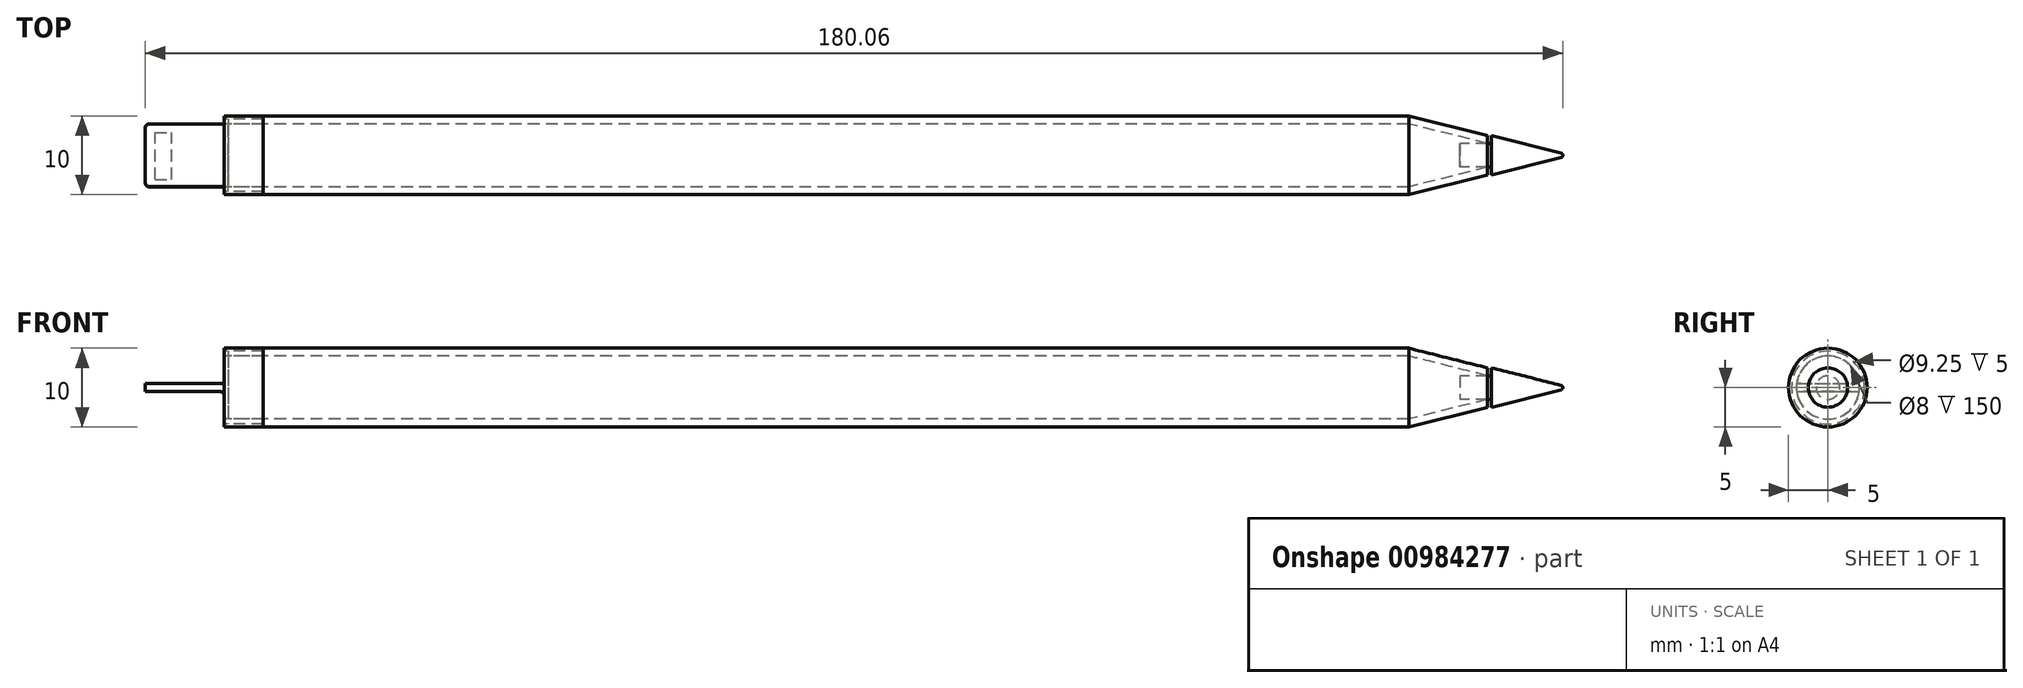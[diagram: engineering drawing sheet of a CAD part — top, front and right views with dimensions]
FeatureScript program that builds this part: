
annotation { "Feature Type Name" : "Feature", "Feature Type Description" : "" }
export const myFeature = defineFeature(function(context is Context, id is Id, definition is map)
    precondition{}
    {
        {
            var Q0;
            Q0=qCreatedBy(makeId("Front.planeOp"),FACE);
            var sketch = newSketch(context, id + "F0", { "sketchPlane" : qUnion([Q0])});
            skLineSegment(sketch, "E0", {"start": v(-75, 0) * mm, "end": v(75, 0) * mm});
            skLineSegment(sketch, "E1", {"start": v(75, -5) * mm, "end": v(-75, -5) * mm});
            skLineSegment(sketch, "E2", {"start": v(-75, -5) * mm, "end": v(-75, -4) * mm});
            skLineSegment(sketch, "E3", {"start": v(75, 0) * mm, "end": v(75, -5) * mm});
            skLineSegment(sketch, "E4", {"start": v(-75, -4) * mm, "end": v(75, -4) * mm});
            skLineSegment(sketch, "E5", {"start": v(75, 0) * mm, "end": v(85, 0) * mm});
            skLineSegment(sketch, "E6", {"start": v(85, 0) * mm, "end": v(85, -2.5) * mm});
            skLineSegment(sketch, "E7", {"start": v(85, -2.5) * mm, "end": v(75, -5) * mm});
            skLineSegment(sketch, "E8.0", {"start": v(85, -1.5) * mm, "end": v(75, -4) * mm});
            skLineSegment(sketch, "E9", {"start": v(85.5, 0) * mm, "end": v(85, 0) * mm});
            skLineSegment(sketch, "E10", {"start": v(85.5, -1.5) * mm, "end": v(85.5, 0) * mm});
            skLineSegment(sketch, "E11", {"start": v(85.5, -1.5) * mm, "end": v(85, -1.5) * mm});
            skLineSegment(sketch, "E12", {"start": v(85, -1.5) * mm, "end": v(85.5, -1.5) * mm});
            skLineSegment(sketch, "E13", {"start": v(85.5, -1.5) * mm, "end": v(85.5, -2.5) * mm});
            skLineSegment(sketch, "E14", {"start": v(85.5, 0) * mm, "end": v(95.5, 0) * mm});
            skLineSegment(sketch, "E15", {"start": v(95.5, 0) * mm, "end": v(85.5, -2.5) * mm});
            skArc(sketch, "E16", {"start": v(94.34, -0.3) * mm, "mid": v(94.5, -0.18) * mm, "end": v(94.56, 0) * mm});
            skLineSegment(sketch, "E17.bottom", {"start": v(85, -1.5) * mm, "end": v(81.5, -1.5) * mm});
            skLineSegment(sketch, "E17.top", {"start": v(85, 0) * mm, "end": v(81.5, 0) * mm});
            skLineSegment(sketch, "E17.left", {"start": v(85, -1.5) * mm, "end": v(85, 0) * mm});
            skLineSegment(sketch, "E17.right", {"start": v(81.5, -1.5) * mm, "end": v(81.5, 0) * mm});
            skLineSegment(sketch, "E18", {"start": v(-75.5, -4.63) * mm, "end": v(-70.5, -4.63) * mm});
            skLineSegment(sketch, "E19", {"start": v(-70.5, -4.63) * mm, "end": v(-70.5, -5) * mm});
            skLineSegment(sketch, "E20", {"start": v(-75.5, -4.63) * mm, "end": v(-75, -4.63) * mm});
            skLineSegment(sketch, "E21", {"start": v(-75.5, -5) * mm, "end": v(-75.5, -4.63) * mm});
            skLineSegment(sketch, "E22", {"start": v(-70.5, 0) * mm, "end": v(-70.5, -4) * mm});
            skLineSegment(sketch, "E23", {"start": v(-75.5, -4) * mm, "end": v(-75, -4) * mm});
            skLineSegment(sketch, "E24", {"start": v(-75.5, 0) * mm, "end": v(-75.5, -4) * mm});
            skLineSegment(sketch, "E25", {"start": v(-75.5, -5) * mm, "end": v(-75, -5) * mm});
            skLineSegment(sketch, "E26", {"start": v(-75.5, 0) * mm, "end": v(-75, 0) * mm});
            skSolve(sketch);
        }
        {
            var Q0;
            {var subQ10=sQuery(id+"F0.wireOp",EDGE,"E19");Q0=makeQuery(id+"F0.imprint","IMPRINT",FACE,{"disambiguationData":[TD([[makeQuery(id+"F0.imprint","IMPRINT",EDGE,{"derivedFrom":subQ10}),1.0]])]});}
            var Q1;
            {var subQ0=sQuery(id+"F0.wireOp",EDGE,"E7");Q1=makeQuery(id+"F0.imprint","IMPRINT",FACE,{"disambiguationData":[TD([[makeQuery(id+"F0.imprint","IMPRINT",EDGE,{"derivedFrom":subQ0}),-1.0]])]});}
            var Q2;
            Q2=sQuery(id+"F0.wireOp",EDGE,"E0");
            revolve(context, id + "F1", {"surfaceOperationType" : NewSurfaceOperationType.NEW, "entities" : qUnion([Q0, Q1]), "axis" : qUnion([Q2]), "revolveType" : RevolveType.FULL});
        }
        {
            var Q0;
            {var subQ4=sQuery(id+"F0.wireOp",EDGE,"E17.bottom");Q0=makeQuery(id+"F0.imprint","IMPRINT",FACE,{"disambiguationData":[TD([[makeQuery(id+"F0.imprint","IMPRINT",EDGE,{"derivedFrom":subQ4}),-1.0]])]});}
            var Q1;
            {var subQ1=sQuery(id+"F0.wireOp",EDGE,"E10");Q1=makeQuery(id+"F0.imprint","IMPRINT",FACE,{"disambiguationData":[TD([[makeQuery(id+"F0.imprint","IMPRINT",EDGE,{"derivedFrom":subQ1}),-1.0]])]});}
            var Q2;
            {var subQ0=sQuery(id+"F0.wireOp",EDGE,"E9");Q2=makeQuery(id+"F0.imprint","IMPRINT",FACE,{"disambiguationData":[TD([[makeQuery(id+"F0.imprint","IMPRINT",EDGE,{"derivedFrom":subQ0}),1.0]])]});}
            var Q3;
            {var subQ10=sQuery(id+"F0.wireOp",EDGE,"E19");Q3=makeQuery(id+"F0.imprint","IMPRINT",FACE,{"disambiguationData":[TD([[makeQuery(id+"F0.imprint","IMPRINT",EDGE,{"derivedFrom":subQ10}),1.0]])]});}
            var Q4;
            Q4=sQuery(id+"F0.wireOp",EDGE,"E0");
            revolve(context, id + "F2", {"surfaceOperationType" : NewSurfaceOperationType.NEW, "entities" : qUnion([Q0, Q1, Q2, Q3]), "axis" : qUnion([Q4]), "revolveType" : RevolveType.FULL});
        }
        {
            var Q0;
            {var subQ3=sQuery(id+"F0.wireOp",EDGE,"E19");Q0=makeQuery(id+"F0.imprint","IMPRINT",FACE,{"disambiguationData":[TD([[makeQuery(id+"F0.imprint","IMPRINT",EDGE,{"derivedFrom":subQ3}),-1.0]])]});}
            var Q1;
            {var subQ4=sQuery(id+"F0.wireOp",EDGE,"E21");Q1=makeQuery(id+"F0.imprint","IMPRINT",FACE,{"disambiguationData":[TD([[makeQuery(id+"F0.imprint","IMPRINT",EDGE,{"derivedFrom":subQ4}),-1.0]])]});}
            var Q2;
            Q2=sQuery(id+"F0.wireOp",EDGE,"E0");
            revolve(context, id + "F3", {"surfaceOperationType" : NewSurfaceOperationType.NEW, "entities" : qUnion([Q0, Q1]), "axis" : qUnion([Q2]), "revolveType" : RevolveType.FULL});
        }
        {
            var Q0;
            Q0=makeQuery(id+"F2.opRevolve","SWEPT_BODY",BODY,{"disambiguationData":[OSD([sQuery(id+"F0.wireOp",EDGE,"E1"),sQuery(id+"F0.wireOp",EDGE,"E2"),sQuery(id+"F0.wireOp",EDGE,"E3"),sQuery(id+"F0.wireOp",EDGE,"E4"),sQuery(id+"F0.wireOp",EDGE,"E18"),sQuery(id+"F0.wireOp",EDGE,"E19")])]});
            deleteBodies(context, id + "F4", {"entities" : qUnion([Q0])});
        }
        {
            var Q0;
            {var subQ1=sQuery(id+"F0.wireOp",EDGE,"E22");Q0=makeQuery(id+"F0.imprint","IMPRINT",FACE,{"disambiguationData":[TD([[makeQuery(id+"F0.imprint","IMPRINT",EDGE,{"derivedFrom":subQ1}),-1.0]])]});}
            var Q1;
            Q1=sQuery(id+"F0.wireOp",EDGE,"E0");
            revolve(context, id + "F5", {"surfaceOperationType" : NewSurfaceOperationType.NEW, "entities" : qUnion([Q0]), "axis" : qUnion([Q1]), "revolveType" : RevolveType.FULL});
        }
        {
            var Q0;
            Q0=makeQuery(id+"F5.opRevolve","SWEPT_FACE",FACE,{"disambiguationData":[OSD([sQuery(id+"F0.wireOp",EDGE,"E24")])]});
            var sketch = newSketch(context, id + "F6", { "sketchPlane" : qUnion([Q0])});
            skLineSegment(sketch, "E27.bottom", {"start": v(4, 0.5) * mm, "end": v(-4, 0.5) * mm});
            skLineSegment(sketch, "E27.top", {"start": v(4, -0.5) * mm, "end": v(-4, -0.5) * mm});
            skLineSegment(sketch, "E27.left", {"start": v(4, 0.5) * mm, "end": v(4, -0.5) * mm});
            skLineSegment(sketch, "E27.right", {"start": v(-4, 0.5) * mm, "end": v(-4, -0.5) * mm});
            skPoint(sketch, "E27.middle", {"position": v(0, 0) * mm});
            skCircle(sketch, "E28.0", {"center": v(0, 0) * mm, "radius": 4 * mm});
            skSolve(sketch);
        }
        {
            var Q0;
            {var subQ0=sQuery(id+"F6.wireOp",EDGE,"E28.0");var subQ1=sQuery(id+"F6.wireOp",EDGE,"E27.bottom");var subQ7=makeQuery(id+"F6.imprint","INTERSECT",VERTEX,{"disambiguationData":[OD(0.0)],"derivedFrom":[subQ1,subQ0]});Q0=makeQuery(id+"F6.imprint","IMPRINT",FACE,{"disambiguationData":[TD([[makeQuery(id+"F6.imprint","IMPRINT",EDGE,{"disambiguationData":[TD([[subQ7,-1.0]])],"derivedFrom":subQ1}),1.0]])]});}
            extrude(context, id + "F7", {"entities" : qUnion([Q0]), "operationType" : NewBodyOperationType.ADD, "depth" : 10 * mm, "offsetDistance" : 25 * mm});
        }
        {
            var Q0;
            Q0=makeQuery(id+"F7.opExtrude","CAP_EDGE",EDGE,{"disambiguationData":[OSD([sQuery(id+"F6.wireOp",EDGE,"E27.top")])],"isStart":true});
            var Q1;
            Q1=makeQuery(id+"F7.opExtrude","CAP_EDGE",EDGE,{"disambiguationData":[OSD([sQuery(id+"F6.wireOp",EDGE,"E27.bottom")])],"isStart":true});
            var Q2;
            {var subQ0=sQuery(id+"F6.wireOp",EDGE,"E28.0");Q2=makeQuery(id+"F7.opExtrude","CAP_EDGE",EDGE,{"disambiguationData":[OSD([subQ0]),TDD([makeQuery(id+"F6.imprint","IMPRINT",EDGE,{"disambiguationData":[TD([[makeQuery(id+"F6.imprint","INTERSECT",VERTEX,{"disambiguationData":[OD(1.0)],"derivedFrom":[sQuery(id+"F6.wireOp",EDGE,"E27.bottom"),subQ0]}),-1.0]])],"derivedFrom":subQ0}),makeQuery(id+"F6.imprint","IMPRINT",EDGE,{"disambiguationData":[TD([[makeQuery(id+"F6.imprint","INTERSECT",VERTEX,{"disambiguationData":[OD(1.0)],"derivedFrom":[sQuery(id+"F6.wireOp",EDGE,"E27.top"),subQ0]}),1.0]])],"derivedFrom":subQ0})])],"isStart":false});}
            var Q3;
            {var subQ0=sQuery(id+"F6.wireOp",EDGE,"E28.0");Q3=makeQuery(id+"F7.opExtrude","CAP_EDGE",EDGE,{"disambiguationData":[OSD([subQ0]),TDD([makeQuery(id+"F6.imprint","IMPRINT",EDGE,{"disambiguationData":[TD([[makeQuery(id+"F6.imprint","INTERSECT",VERTEX,{"disambiguationData":[OD(0.0)],"derivedFrom":[sQuery(id+"F6.wireOp",EDGE,"E27.top"),subQ0]}),-1.0]])],"derivedFrom":subQ0}),makeQuery(id+"F6.imprint","IMPRINT",EDGE,{"disambiguationData":[TD([[makeQuery(id+"F6.imprint","INTERSECT",VERTEX,{"disambiguationData":[OD(0.0)],"derivedFrom":[sQuery(id+"F6.wireOp",EDGE,"E27.bottom"),subQ0]}),1.0]])],"derivedFrom":subQ0})])],"isStart":false});}
            fillet(context, id + "F8", {"entities" : qUnion([Q0, Q1, Q2, Q3]), "radius" : 0.5 * mm, "tangentPropagation" : true, "allowEdgeOverflow" : false});
        }
        {
            var Q0;
            Q0=makeQuery(id+"F7.opExtrude","SWEPT_FACE",FACE,{"disambiguationData":[OSD([sQuery(id+"F6.wireOp",EDGE,"E27.top")])]});
            var sketch = newSketch(context, id + "F9", { "sketchPlane" : qUnion([Q0])});
            skLineSegment(sketch, "E29.bottom", {"start": v(-84.27, 3.08) * mm, "end": v(-82.17, 3.08) * mm});
            skLineSegment(sketch, "E29.top", {"start": v(-84.27, -2.89) * mm, "end": v(-82.17, -2.89) * mm});
            skLineSegment(sketch, "E29.left", {"start": v(-84.27, 3.08) * mm, "end": v(-84.27, -2.89) * mm});
            skLineSegment(sketch, "E29.right", {"start": v(-82.17, 3.08) * mm, "end": v(-82.17, -2.89) * mm});
            skSolve(sketch);
        }
        {
            var Q0;
            Q0=makeQuery(id+"F9.imprint","IMPRINT",FACE,{"disambiguationData":[TD([[makeQuery(id+"F9.imprint","IMPRINT",EDGE,{"derivedFrom":sQuery(id+"F9.wireOp",EDGE,"E29.bottom")}),-1.0]])]});
            extrude(context, id + "F10", {"entities" : qUnion([Q0]), "operationType" : NewBodyOperationType.REMOVE, "oppositeDirection" : true, "depth" : .1 * mm, "offsetDistance" : 25 * mm});
        }
    });
